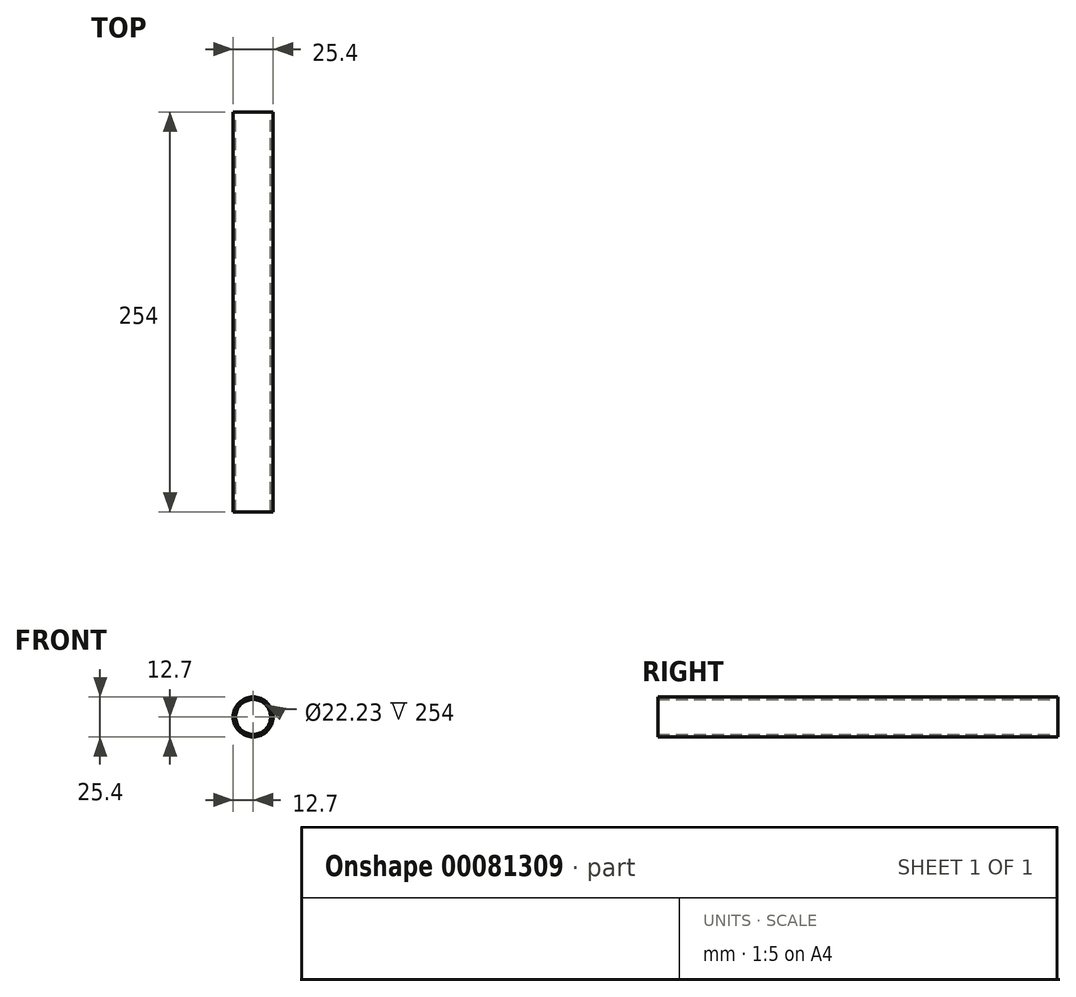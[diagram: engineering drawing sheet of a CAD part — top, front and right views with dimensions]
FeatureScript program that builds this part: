
annotation { "Feature Type Name" : "Feature", "Feature Type Description" : "" }
export const myFeature = defineFeature(function(context is Context, id is Id, definition is map)
    precondition{}
    {
        {
            var Q0;
            Q0=qCreatedBy(makeId("Front.planeOp"),FACE);
            var sketch = newSketch(context, id + "F0", { "sketchPlane" : qUnion([Q0])});
            skCircle(sketch, "E0", {"center": v(0, 0) * mm, "radius": 12.7 * mm});
            skCircle(sketch, "E1", {"center": v(0, 0) * mm, "radius": 11.11 * mm});
            skSolve(sketch);
        }
        {
            var Q0;
            Q0 = qSketchRegion(id + "F0", true);
            extrude(context, id + "F1", {"entities" : qUnion([Q0]), "depth" : 254 * mm});
        }
    });
